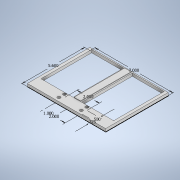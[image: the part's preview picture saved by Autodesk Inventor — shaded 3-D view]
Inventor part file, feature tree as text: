
AUTODESK INVENTOR PART (.ipt)
format: ipt  version: 2020 (Build 240168000, 168)  size: 153,088 bytes
history: native  units: in
note: dims shown in document units (in); Inventor stores cm internally (conversion verified against a paired STEP export)
features: sketch x3, extrude x3, hole x1
ambient origin geometry x8: Origin, YZ Plane, XZ Plane, XY Plane, X Axis, Y Axis, Z Axis, Center Point
bodies: Solid1 (feature_tree)
feature tree (7):
  sketch  "Sketch1"  dims[d0=7.0in d1=5.6in]
  extrude  "Extrusion1"  Depth=5.6in
  hole  "Hole1"  [1 undecoded]
  extrude  "Extrusion2"  Depth=0.05in
  extrude  "Extrusion4"  Depth=0.05in
  sketch  "Sketch2"  dims[d2=1.0in d3=2.0in]
  sketch  "Sketch3"  dims[d4=0.325in d5=0.5in d6=2.0in d7=0.25in d8=0.0in d9=0.266in d10=0.75in d11=0.438in d12=0.25in d13=0.5635in d14=1.0in d15=0.8108in d16=0.25in d17=0.1in d18=2.8654in d19=4.5299in d20=0.25in d21=2.865in d22=4.5299in d23=0.25in d24=0.0in d26=0.1in d27=0.1in d30=0.1in d31=0.1in d32=0.05in d33=0.0in]
note: 1 required parameter value undecoded (feature->parameter linkage not recoverable at this tier; creation-order binding heuristic only, values carry confidence <= 0.55)
